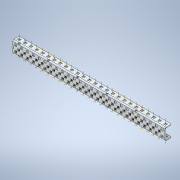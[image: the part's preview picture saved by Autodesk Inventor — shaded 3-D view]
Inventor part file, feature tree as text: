
AUTODESK INVENTOR PART (.ipt)
format: ipt  version: 2020 (Build 240168000, 168)  size: 1,453,056 bytes
history: native  units: in
note: dims shown in document units (in); Inventor stores cm internally (conversion verified against a paired STEP export)
features: other x133, plane x7, pattern_linear x4, split x1, sheet_metal_op x1
ambient origin geometry x8: Origin, YZ Plane, XZ Plane, XY Plane, X Axis, Y Axis, Z Axis, Center Point
bodies: Solid1 (feature_tree)
feature tree (146):
  other  "Work Axis1"
  pattern_linear  "Rectangular Pattern1"  Count1=26 Spacing1=0.5in
  other  "Work Axis72"
  pattern_linear  "Rectangular Pattern2"  Count1=26 Spacing1=0.5in
  pattern_linear  "Rectangular Pattern3"  Count1=26 Spacing1=0.5in
  other  "Work Axis141"
  pattern_linear  "Rectangular Pattern4"  Count1=25 Spacing1=0.5in
  plane  "Work Plane7"
  split  "Split1"
  plane  "Work Plane1"
  plane  "Work Plane2"
  other  "Work Point1"
  other  "Work Axis2"
  other  "Work Axis3"
  other  "Work Axis4"
  other  "Work Axis5"
  other  "Work Axis6"
  other  "Work Axis7"
  other  "Work Axis8"
  other  "Work Axis9"
  other  "Work Axis10"
  other  "Work Axis11"
  other  "Work Axis12"
  other  "Work Axis13"
  other  "Work Axis14"
  other  "Work Axis15"
  other  "Work Axis16"
  other  "Work Axis17"
  other  "Work Axis18"
  other  "Work Axis19"
  other  "Work Axis20"
  other  "Work Axis21"
  other  "Work Axis22"
  other  "Work Axis23"
  other  "Work Axis24"
  other  "Work Axis25"
  other  "Work Axis26"
  other  "Work Axis36"
  other  "Work Axis37"
  other  "Work Axis38"
  other  "Work Axis39"
  other  "Work Axis40"
  other  "Work Axis41"
  other  "Work Axis42"
  other  "Work Axis43"
  other  "Work Axis44"
  other  "Work Axis45"
  other  "Work Axis46"
  other  "Work Axis47"
  other  "Work Axis48"
  other  "Work Axis49"
  other  "Work Axis50"
  other  "Work Axis51"
  other  "Work Axis52"
  other  "Work Axis53"
  other  "Work Axis54"
  other  "Work Axis55"
  other  "Work Axis56"
  other  "Work Axis57"
  other  "Work Axis58"
  other  "Work Axis59"
  other  "Work Axis60"
  other  "Work Axis61"
  plane  "Work Plane3"
  plane  "Work Plane4"
  other  "Work Point2"
  other  "Work Axis71"
  other  "Work Point3"
  other  "Work Axis73"
  other  "Work Axis74"
  other  "Work Axis75"
  other  "Work Axis76"
  other  "Work Axis77"
  other  "Work Axis78"
  other  "Work Axis79"
  other  "Work Axis80"
  other  "Work Axis81"
  other  "Work Axis82"
  other  "Work Axis83"
  other  "Work Axis84"
  other  "Work Axis85"
  other  "Work Axis86"
  other  "Work Axis87"
  other  "Work Axis88"
  other  "Work Axis89"
  other  "Work Axis90"
  other  "Work Axis91"
  other  "Work Axis92"
  other  "Work Axis93"
  other  "Work Axis94"
  other  "Work Axis95"
  other  "Work Axis96"
  other  "Work Axis97"
  other  "Work Axis107"
  other  "Work Axis108"
  other  "Work Axis109"
  other  "Work Axis110"
  other  "Work Axis111"
  other  "Work Axis112"
  other  "Work Axis113"
  other  "Work Axis114"
  other  "Work Axis115"
  other  "Work Axis116"
  other  "Work Axis117"
  other  "Work Axis118"
  other  "Work Axis119"
  other  "Work Axis120"
  other  "Work Axis121"
  other  "Work Axis122"
  other  "Work Axis123"
  other  "Work Axis124"
  other  "Work Axis125"
  other  "Work Axis126"
  other  "Work Axis127"
  other  "Work Axis128"
  other  "Work Axis129"
  other  "Work Axis130"
  other  "Work Axis131"
  plane  "Work Plane5"
  plane  "Work Plane6"
  other  "Work Point4"
  other  "Work Axis142"
  other  "Work Axis143"
  other  "Work Axis144"
  other  "Work Axis145"
  other  "Work Axis146"
  other  "Work Axis147"
  other  "Work Axis148"
  other  "Work Axis149"
  other  "Work Axis150"
  other  "Work Axis151"
  other  "Work Axis152"
  other  "Work Axis153"
  other  "Work Axis154"
  other  "Work Axis155"
  other  "Work Axis156"
  other  "Work Axis157"
  other  "Work Axis158"
  other  "Work Axis159"
  other  "Work Axis160"
  other  "Work Axis161"
  other  "Work Axis162"
  other  "Work Axis163"
  other  "Work Axis164"
  other  "Work Axis165"
  sheet_metal_op  "Fold1"
